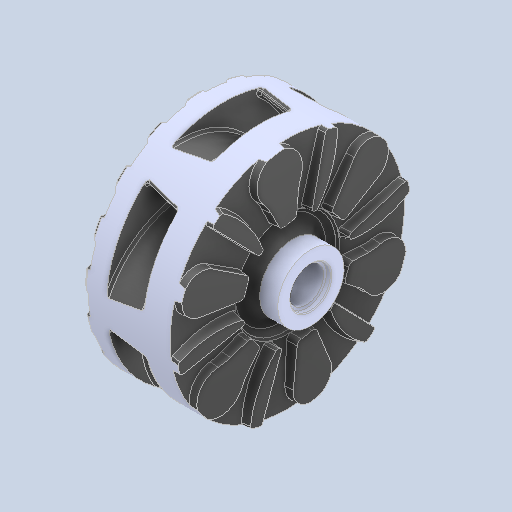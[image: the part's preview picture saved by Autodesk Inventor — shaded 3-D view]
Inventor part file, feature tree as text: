
AUTODESK INVENTOR PART (.ipt)
format: ipt  version: 2024.1 (Build 281209000, 209)  size: 2,956,800 bytes
history: native  units: in
note: dims shown in document units (in); Inventor stores cm internally (conversion verified against a paired STEP export)
features: fillet x1
ambient origin geometry x8: Origin, YZ Plane, XZ Plane, XY Plane, X Axis, Y Axis, Z Axis, Center Point
bodies: Solid1 (feature_tree)
feature tree (1):
  fillet  "Fillet13"  [1 undecoded]
note: 1 required parameter value undecoded (feature->parameter linkage not recoverable at this tier; creation-order binding heuristic only, values carry confidence <= 0.55)
